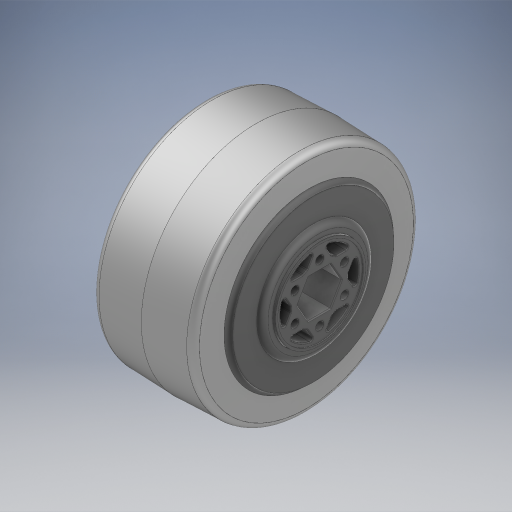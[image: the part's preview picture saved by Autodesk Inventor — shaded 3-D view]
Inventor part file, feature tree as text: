
AUTODESK INVENTOR PART (.ipt)
format: ipt  version: 2024.2 (Build 282272000, 272)  size: 1,599,488 bytes
history: native  units: in
note: dims shown in document units (in); Inventor stores cm internally (conversion verified against a paired STEP export)
features: revolve x1
ambient origin geometry x8: Origin, YZ Plane, XZ Plane, XY Plane, X Axis, Y Axis, Z Axis, Center Point
bodies: Solid1 (feature_tree)
feature tree (1):
  revolve  "Revolve1"  [1 undecoded]
note: 1 required parameter value undecoded (feature->parameter linkage not recoverable at this tier; creation-order binding heuristic only, values carry confidence <= 0.55)
